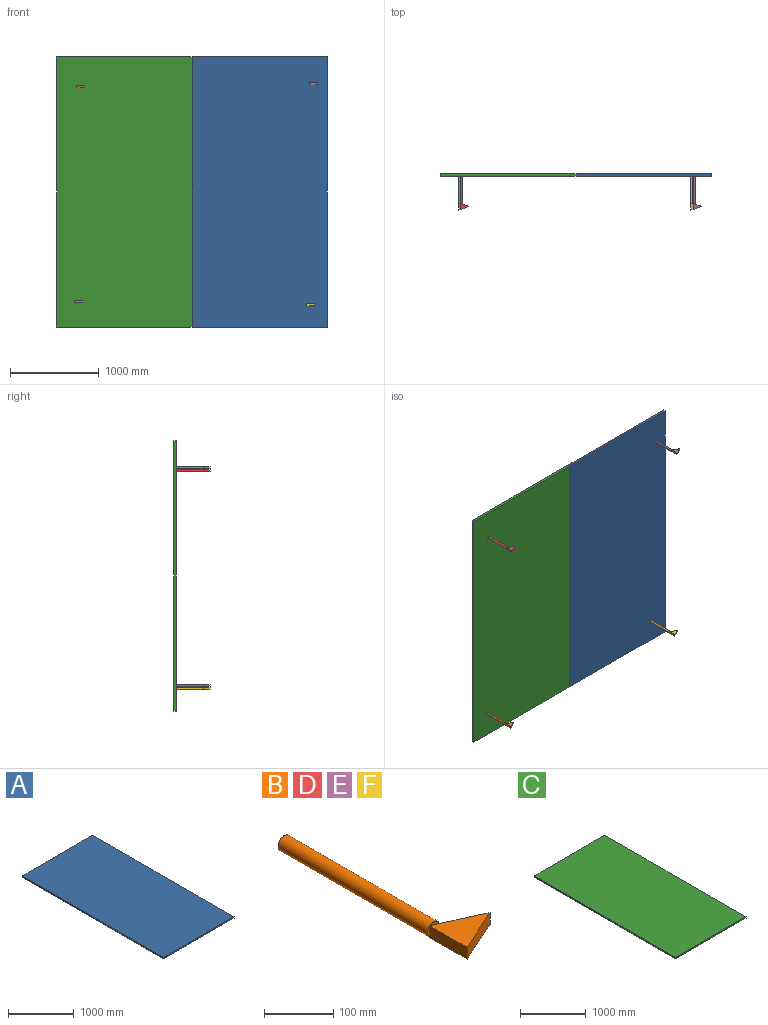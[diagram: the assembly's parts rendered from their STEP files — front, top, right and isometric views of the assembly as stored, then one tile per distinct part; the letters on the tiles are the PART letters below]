
ASSEMBLY  parts=6 mates=5
PART A: 6 faces, bbox 1524x3048x25.4 mm
  f0: plane 1524x25.4mm, normal (0,1,0), area 38709.6mm2, adj f1,f3,f4,f5
  f1: plane 3048x25.4mm, normal (-1,0,0), area 77419.2mm2, adj f0,f2,f4,f5
  f2: plane 1524x25.4mm, normal (0,-1,0), area 38709.6mm2, adj f1,f3,f4,f5
  f3: plane 3048x25.4mm, normal (1,0,0), area 77419.2mm2, adj f0,f2,f4,f5
  f4: plane 3048x1524mm, normal (0,0,-1), area 4645152mm2, adj f0,f1,f2,f3
  f5: plane 3048x1524mm, normal (0,0,1), area 4645152mm2, adj f0,f1,f2,f3
PART B: 10 faces, bbox 89.7x381x25.4 mm
  f0: plane 84.9x76.2mm, normal (0,0,1), area 3255.4mm2, adj f4,f7,f8,f9
  f1: plane 84.9x76.2mm, normal (0,0,-1), area 3255.4mm2, adj f6,f7,f8,f9
  f2: plane 19.89x4.8mm, normal (0,-1,0), area 66.6mm2, adj f3,f7
  f3: cylinder r=12.7mm len=304.8mm, axis (0,1,0), area 24322mm2, adj f2,f4,f5,f6
  f4: plane 25.4x20.6mm, normal (0,-1,0), area 417.9mm2, adj f0,f3,f8
  f5: plane 25.4x25.4mm, normal (0,1,0), area 506.7mm2, adj f3
  f6: plane 1.09x0.78mm, normal (0,1,0), area 0.4mm2, adj f1,f3,f7
  f7: plane 76.2x20.67mm, normal (-1,0,0), area 1575.1mm2, adj f0,f1,f2,f6,f9
  f8: plane 83.81x38.1mm, normal (0.41,0.91,0), area 1902.9mm2, adj f0,f1,f4,f9
  f9: plane 84.9x38.1mm, normal (0.41,-0.91,0), area 1923.5mm2, adj f0,f1,f7,f8
PART C: 6 faces, bbox 1524x3048x25.4 mm
  f0: plane 1524x25.4mm, normal (0,1,0), area 38709.6mm2, adj f1,f3,f4,f5
  f1: plane 3048x25.4mm, normal (-1,0,0), area 77419.2mm2, adj f0,f2,f4,f5
  f2: plane 1524x25.4mm, normal (0,-1,0), area 38709.6mm2, adj f1,f3,f4,f5
  f3: plane 3048x25.4mm, normal (1,0,0), area 77419.2mm2, adj f0,f2,f4,f5
  f4: plane 3048x1524mm, normal (0,0,1), area 4645152mm2, adj f0,f1,f2,f3
  f5: plane 3048x1524mm, normal (0,0,-1), area 4645152mm2, adj f0,f1,f2,f3
PART D: same geometry as B
PART E: same geometry as B
PART F: same geometry as B
PLACE A rot(axis=(-1,0,0),90deg) t=(-2480.01,-1199.04,2451.23)mm
PLACE B t=(-4753.69,-1199.04,1545.7)mm
PLACE C rot(axis=(-1,0,0),90deg) t=(-2480.01,-1199.04,2451.23)mm
PLACE D t=(-4732.79,-1199.04,3965.12)mm
PLACE E t=(-2106.76,-1199.04,3998.68)mm
PLACE F t=(-2138.34,-1199.04,1509.16)mm
MATE planar D.f3 <-> C.f5  axis (0,1,0) through (-4732.79,-1199.04,3965.12)mm
MATE planar C.f5 <-> B.f3  axis (0,-1,0) through (-4203.68,-1199.04,2779.4)mm
MATE planar A.f4 <-> E.f3  axis (0,-1,0) through (-2679.68,-1199.04,2779.4)mm
MATE planar A.f4 <-> F.f3  axis (0,-1,0) through (-2679.68,-1199.04,2779.4)mm
MATE fastened A.f1 <-> C.f3  axis (-1,0,0) through (-3441.68,-1173.64,1255.4)mm
